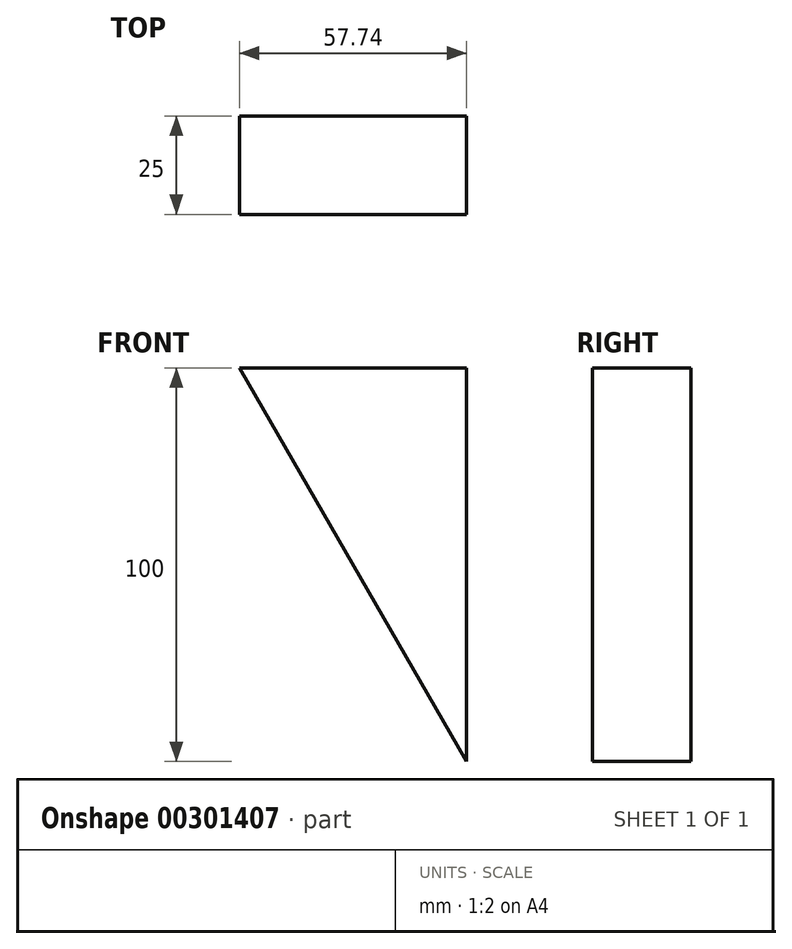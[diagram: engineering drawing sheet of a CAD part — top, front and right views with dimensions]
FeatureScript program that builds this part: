
annotation { "Feature Type Name" : "Feature", "Feature Type Description" : "" }
export const myFeature = defineFeature(function(context is Context, id is Id, definition is map)
    precondition{}
    {
        {
            var Q0;
            Q0=qCreatedBy(makeId("Front.planeOp"),FACE);
            var sketch = newSketch(context, id + "F0", { "sketchPlane" : qUnion([Q0])});
            skLineSegment(sketch, "E0", {"start": v(0, 0) * mm, "end": v(300, 0) * mm});
            skLineSegment(sketch, "E1", {"start": v(0, 100) * mm, "end": v(0, 0) * mm});
            skLineSegment(sketch, "E2", {"start": v(0, 100) * mm, "end": v(300, 100) * mm});
            skLineSegment(sketch, "E3", {"start": v(300, 100) * mm, "end": v(300, 0) * mm});
            skLineSegment(sketch, "E4", {"start": v(0, 0) * mm, "end": v(173.2, 100) * mm});
            skLineSegment(sketch, "E5", {"start": v(173.2, 100) * mm, "end": v(142.26, 0) * mm});
            skLineSegment(sketch, "E6", {"start": v(142.26, 0) * mm, "end": v(242.26, 100) * mm});
            skLineSegment(sketch, "E7", {"start": v(242.26, 100) * mm, "end": v(300, 0) * mm});
            skLineSegment(sketch, "E8.bottom", {"start": v(300, 100) * mm, "end": v(350, 100) * mm});
            skLineSegment(sketch, "E8.top", {"start": v(300, 0) * mm, "end": v(350, 0) * mm});
            skLineSegment(sketch, "E8.right", {"start": v(350, 100) * mm, "end": v(350, 0) * mm});
            skSolve(sketch);
        }
        {
            var Q0;
            {var subQ2=sQuery(id+"F0.wireOp",EDGE,"E7");Q0=makeQuery(id+"F0.imprint","IMPRINT",FACE,{"disambiguationData":[TD([[makeQuery(id+"F0.imprint","IMPRINT",EDGE,{"derivedFrom":subQ2}),1.0]])]});}
            extrude(context, id + "F1", {"entities" : qUnion([Q0]), "depth" : 25 * mm});
        }
    });
